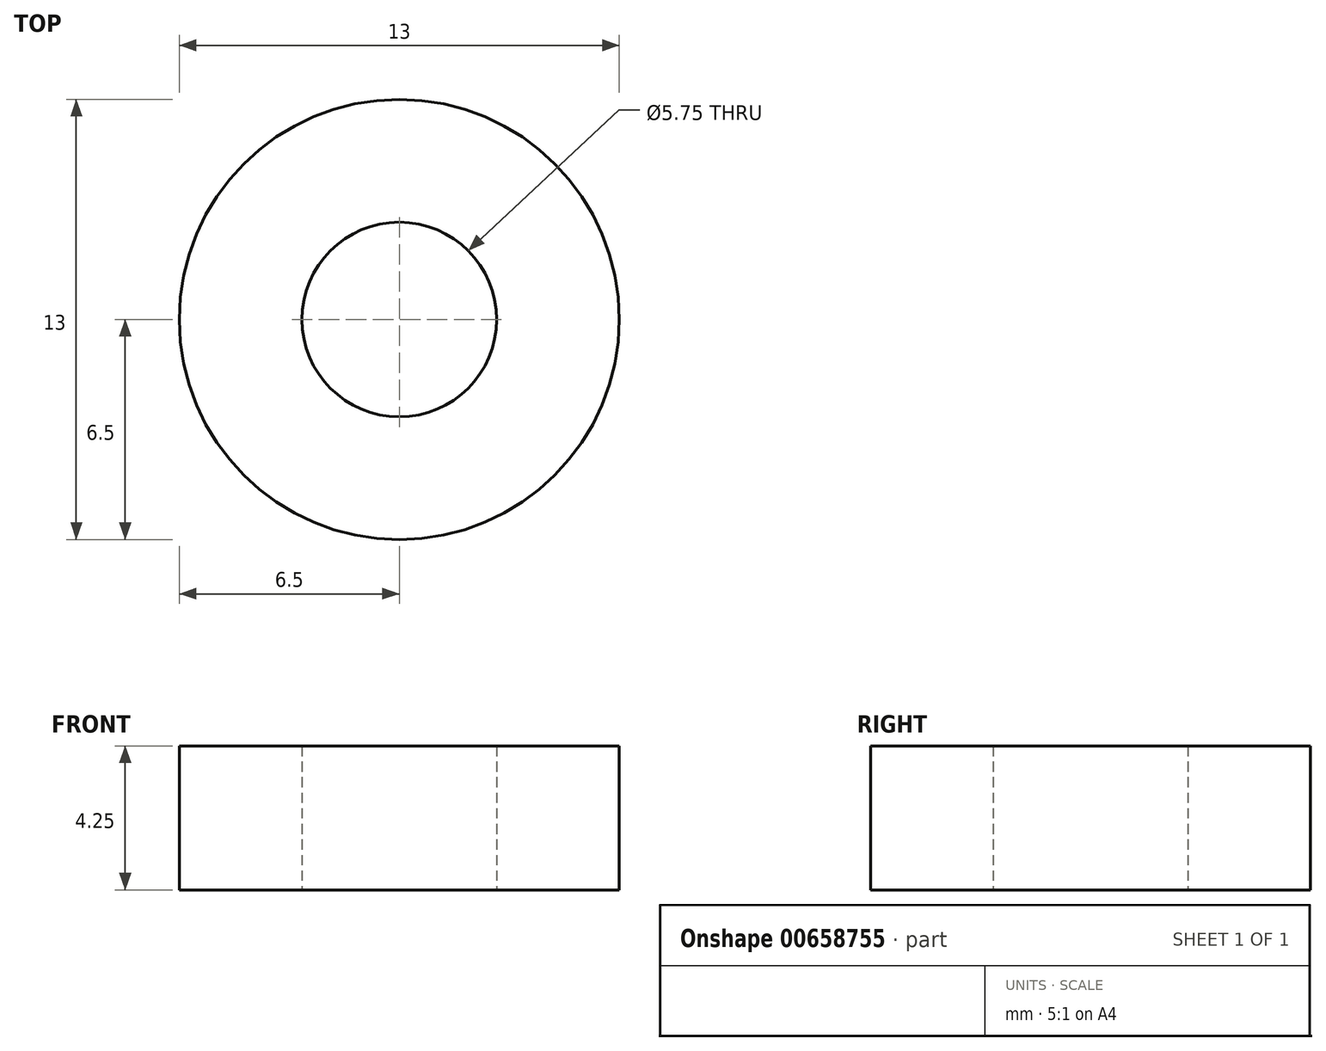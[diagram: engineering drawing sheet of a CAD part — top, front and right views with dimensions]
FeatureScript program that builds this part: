
annotation { "Feature Type Name" : "Feature", "Feature Type Description" : "" }
export const myFeature = defineFeature(function(context is Context, id is Id, definition is map)
    precondition{}
    {
        {
            var Q0;
            Q0=qCreatedBy(makeId("Top.planeOp"),FACE);
            var sketch = newSketch(context, id + "F0", { "sketchPlane" : qUnion([Q0])});
            skCircle(sketch, "E0", {"center": v(0, 0) * mm, "radius": 6.5 * mm});
            skCircle(sketch, "E1", {"center": v(0, 0) * mm, "radius": 2.88 * mm});
            skSolve(sketch);
        }
        {
            var Q0;
            Q0=makeQuery(id+"F0.imprint","IMPRINT",FACE,{"disambiguationData":[TD([[makeQuery(id+"F0.imprint","IMPRINT",EDGE,{"derivedFrom":sQuery(id+"F0.wireOp",EDGE,"E0")}),1.0]])]});
            extrude(context, id + "F1", {"entities" : qUnion([Q0]), "depth" : 4.25 * mm, "offsetDistance" : 25 * mm});
        }
    });
